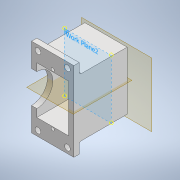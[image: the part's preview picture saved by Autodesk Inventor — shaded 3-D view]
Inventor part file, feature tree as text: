
AUTODESK INVENTOR PART (.ipt)
format: ipt  version: 2022 (Build 260153000, 153)  size: 158,720 bytes
history: native  units: in
note: dims shown in document units (in); Inventor stores cm internally (conversion verified against a paired STEP export)
features: extrude x3, sketch x3, plane x2, other x2, fillet x1, mirror x1, reference x1
ambient origin geometry x8: Origin, YZ Plane, XZ Plane, XY Plane, X Axis, Y Axis, Z Axis, Center Point
bodies: Solid1 (feature_tree)
feature tree (13):
  plane  "Work Plane1"
  extrude  "Extrusion1"  Depth=0.1181in
  extrude  "Extrusion2"  Depth=0.1969in
  extrude  "Extrusion3"  Depth=0.0787in
  fillet  "Fillet1"  Radius=1.9685in
  plane  "Work Plane2"
  mirror  "Mirror1"
  sketch  "Sketch1"  dims[d0=0.0197in d2=0.1181in]
  reference  "Reference1"
  sketch  "Sketch2"  dims[d3=0.1181in d4=0.1969in]
  sketch  "Sketch3"  dims[d5=1.9685in d6=0.0in d7=1.1811in d8=1.9685in d9=0.0in d10=0.2087in d12=0.2362in d13=0.3937in d14=0.1969in d15=0.0in d16=0.0787in]
  other  "Assembly1"
  other  "peristaltic pump:1"
